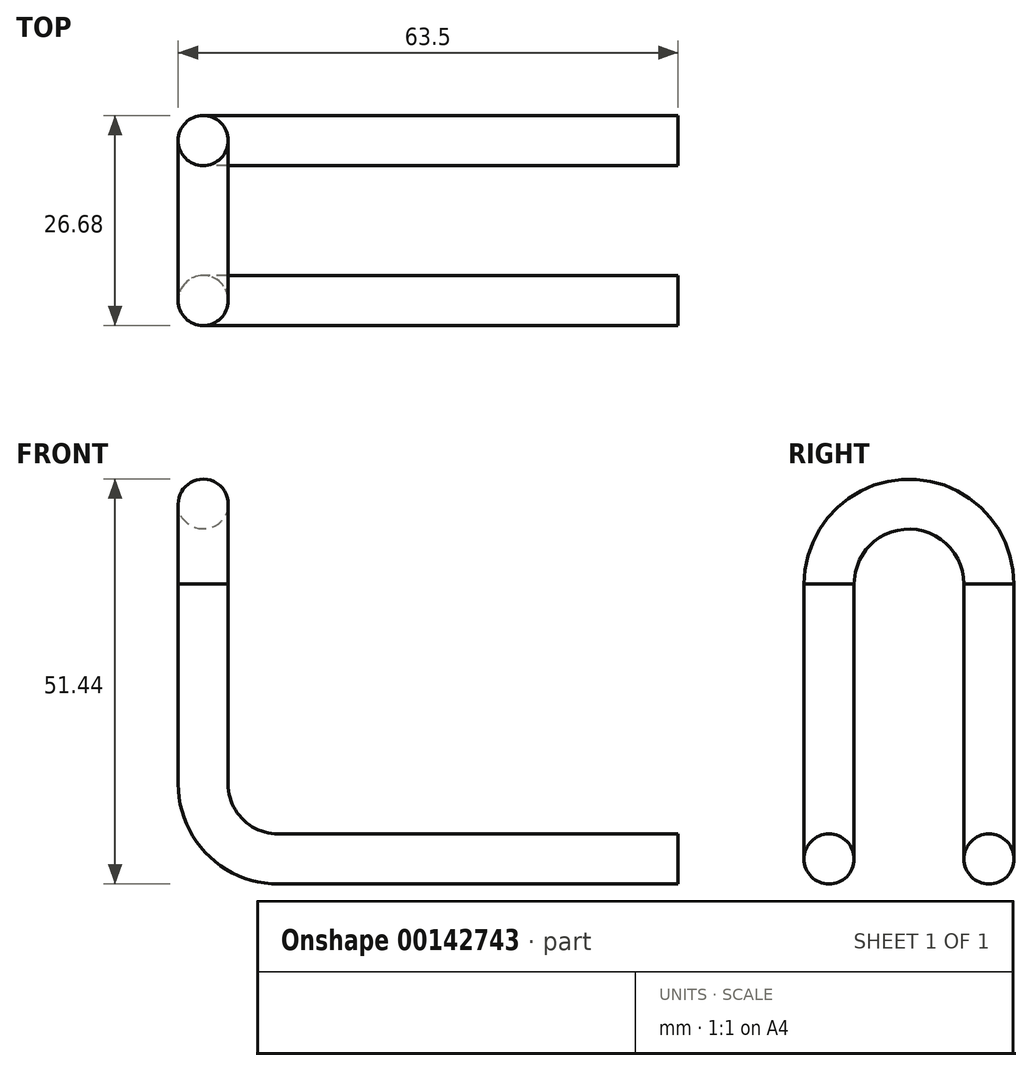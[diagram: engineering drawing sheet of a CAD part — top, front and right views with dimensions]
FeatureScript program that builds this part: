
annotation { "Feature Type Name" : "Feature", "Feature Type Description" : "" }
export const myFeature = defineFeature(function(context is Context, id is Id, definition is map)
    precondition{}
    {
        {
            var Q0;
            Q0=qCreatedBy(makeId("Front.planeOp"),FACE);
            var sketch = newSketch(context, id + "F0", { "sketchPlane" : qUnion([Q0])});
            skArc(sketch, "E0", {"start": v(-9.53, 0) * mm, "mid": v(-6.74, -6.74) * mm, "end": v(0, -9.53) * mm});
            skLineSegment(sketch, "E1", {"start": v(-9.53, 0) * mm, "end": v(-9.53, 25.4) * mm});
            skLineSegment(sketch, "E2", {"start": v(0, -9.53) * mm, "end": v(50.8, -9.52) * mm});
            skSolve(sketch);
        }
        {
            var Q0;
            Q0=qCreatedBy(makeId("Right.planeOp"),FACE);
            var Q1;
            Q1=sQuery(id+"F0.wireOp",VERTEX,"E2.end");
            cPlane(context, id + "F1", {"entities" : qUnion([Q0, Q1]), "cplaneType" : CPlaneType.PLANE_POINT, "offset" : 25.4 * mm, "width" : 152.4 * mm, "height" : 152.4 * mm});
        }
        {
            var Q0;
            Q0=qCreatedBy(id+"F1.planeOp",FACE);
            var sketch = newSketch(context, id + "F2", { "sketchPlane" : qUnion([Q0])});
            skCircle(sketch, "E3", {"center": v(0, -9.52) * mm, "radius": 3.18 * mm});
            skSolve(sketch);
        }
        {
            var Q0;
            Q0 = qSketchRegion(id + "F2", true);
            var Q1;
            Q1 = qConstructionFilter(qBodyType(qCreatedBy(id + "F2" ,EDGE), BodyType.WIRE), ConstructionObject.NO);
            var Q2;
            Q2 = qConstructionFilter(qBodyType(qCreatedBy(id + "F0" ,EDGE), BodyType.WIRE), ConstructionObject.NO);
            sweep(context, id + "F3", {"profiles" : qUnion([Q0]), "surfaceProfiles" : qUnion([Q1]), "path" : qUnion([Q2])});
        }
        {
            var Q0;
            Q0=qCreatedBy(makeId("Front.planeOp"),FACE);
            cPlane(context, id + "F4", {"entities" : qUnion([Q0]), "cplaneType" : CPlaneType.OFFSET, "offset" : 10.16 * mm, "oppositeDirection" : true, "width" : 152.4 * mm, "height" : 152.4 * mm});
        }
        {
            var Q0;
            Q0=makeQuery(id+"F3.opSweep","SWEPT_BODY",BODY,{"disambiguationData":[OSD([sQuery(id+"F0.wireOp",EDGE,"E1"),sQuery(id+"F2.wireOp",EDGE,"E3")])]});
            var Q1;
            Q1=qCreatedBy(id+"F4.planeOp",FACE);
            mirror(context, id + "F5", {"entities" : qUnion([Q0]), "mirrorPlane" : qUnion([Q1])});
        }
        {
            var Q0;
            Q0=makeQuery(id+"F3.opSweep","CAP_FACE",FACE,{"disambiguationData":[OSD([sQuery(id+"F0.wireOp",VERTEX,"E1.end"),sQuery(id+"F2.wireOp",EDGE,"E3")])],"isStart":false});
            var sketch = newSketch(context, id + "F6", { "sketchPlane" : qUnion([Q0])});
            skCircle(sketch, "E4.0", {"center": v(-9.53, 0) * mm, "radius": 3.18 * mm});
            skLineSegment(sketch, "E5", {"start": v(-48.08, 10.16) * mm, "end": v(-9.53, 10.16) * mm, "construction": true});
            skCircle(sketch, "E6.0", {"center": v(-9.53, 20.32) * mm, "radius": 3.18 * mm, "construction": true});
            skLineSegment(sketch, "E7", {"start": v(-9.53, 0) * mm, "end": v(-9.53, 20.32) * mm, "construction": true});
            skSolve(sketch);
        }
        {
            var Q0;
            Q0 = qSketchRegion(id + "F6", true);
            var Q1;
            Q1=sQuery(id+"F6.wireOp",EDGE,"E5");
            revolve(context, id + "F7", {"entities" : qUnion([Q0]), "axis" : qUnion([Q1]), "revolveType" : RevolveType.ONE_DIRECTION, "oppositeDirection" : true, "angle" : 180 * degree});
        }
    });
